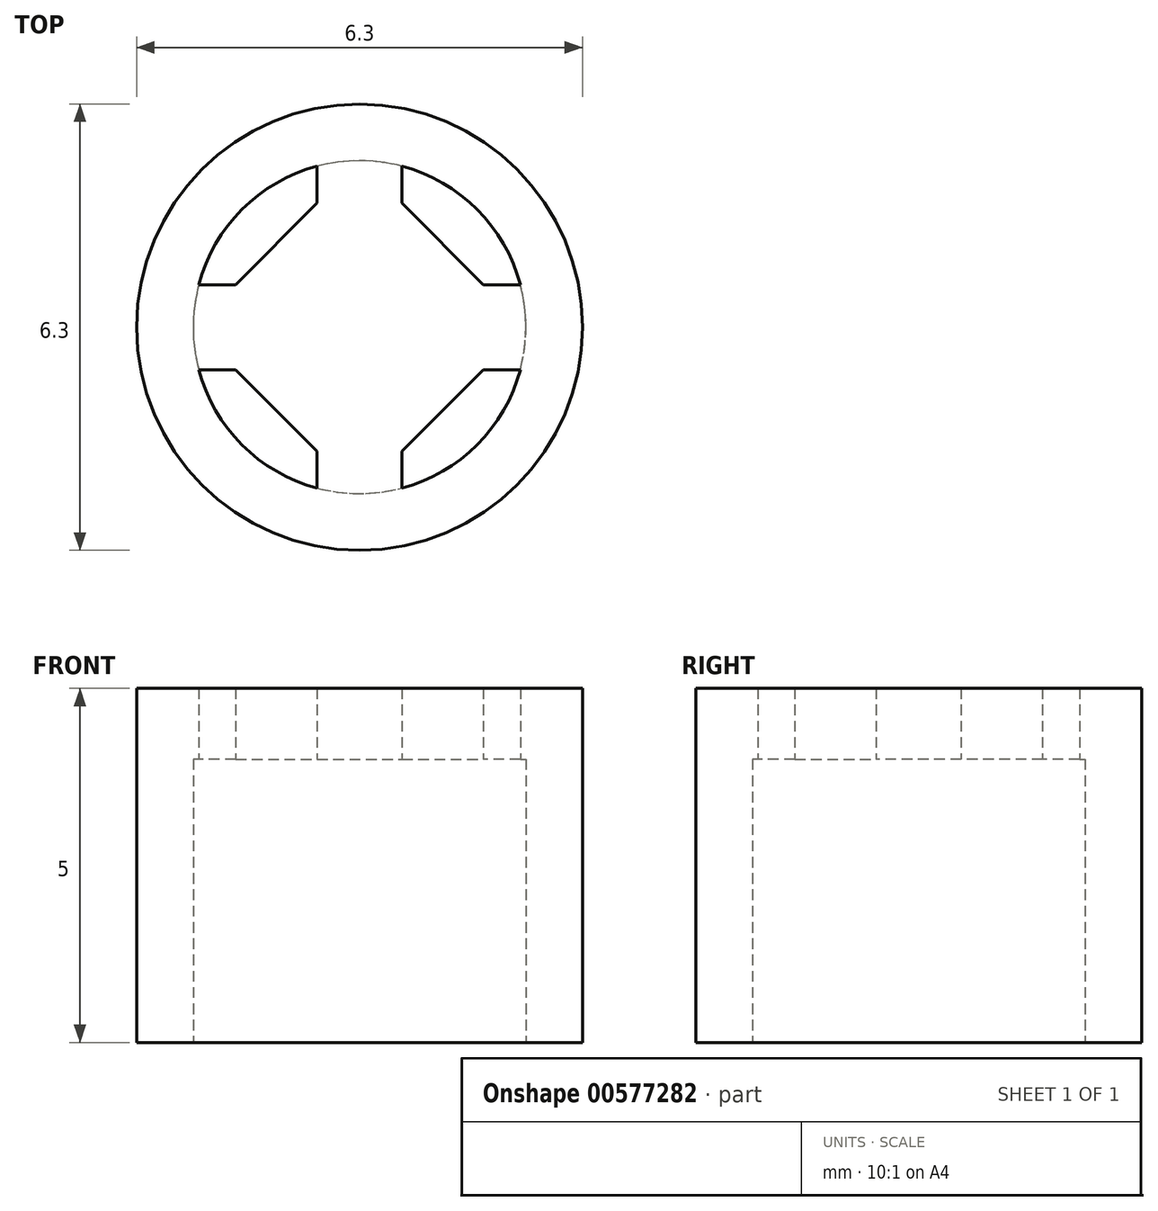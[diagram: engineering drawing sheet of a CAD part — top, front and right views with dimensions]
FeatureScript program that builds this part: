
annotation { "Feature Type Name" : "Feature", "Feature Type Description" : "" }
export const myFeature = defineFeature(function(context is Context, id is Id, definition is map)
    precondition{}
    {
        {
            var Q0;
            Q0=qCreatedBy(makeId("Top.planeOp"),FACE);
            var sketch = newSketch(context, id + "F0", { "sketchPlane" : qUnion([Q0])});
            skCircle(sketch, "E0", {"center": v(0, 0) * mm, "radius": 3.15 * mm});
            skCircle(sketch, "E1.0", {"center": v(0, 0) * mm, "radius": 2.35 * mm});
            skSolve(sketch);
        }
        {
            var Q0;
            Q0=makeQuery(id+"F0.imprint","IMPRINT",FACE,{"disambiguationData":[TD([[makeQuery(id+"F0.imprint","IMPRINT",EDGE,{"derivedFrom":sQuery(id+"F0.wireOp",EDGE,"E0")}),1.0]])]});
            extrude(context, id + "F1", {"entities" : qUnion([Q0]), "depth" : 4 * mm, "offsetDistance" : 25 * mm});
        }
        {
            var Q0;
            Q0=makeQuery(id+"F1.opExtrude","CAP_FACE",FACE,{"disambiguationData":[OSD([sQuery(id+"F0.wireOp",EDGE,"E0"),sQuery(id+"F0.wireOp",EDGE,"E1.0")])],"isStart":false});
            var sketch = newSketch(context, id + "F2", { "sketchPlane" : qUnion([Q0])});
            skArc(sketch, "E2.0", {"start": v(-0.6, 2.27) * mm, "mid": v(-1.66, 1.66) * mm, "end": v(-2.27, 0.6) * mm});
            skLineSegment(sketch, "E3", {"start": v(-0.6, 1.75) * mm, "end": v(-1.75, 0.6) * mm});
            skLineSegment(sketch, "E4", {"start": v(-1.75, -0.6) * mm, "end": v(-0.6, -1.75) * mm});
            skLineSegment(sketch, "E5", {"start": v(0.6, -1.75) * mm, "end": v(1.75, -0.6) * mm});
            skLineSegment(sketch, "E6", {"start": v(1.75, 0.6) * mm, "end": v(0.6, 1.75) * mm});
            skLineSegment(sketch, "E7.left", {"start": v(0.6, 2.27) * mm, "end": v(0.6, 1.75) * mm});
            skLineSegment(sketch, "E7.right", {"start": v(-0.6, 2.27) * mm, "end": v(-0.6, 1.75) * mm});
            skLineSegment(sketch, "E8.bottom", {"start": v(2.27, 0.6) * mm, "end": v(1.75, 0.6) * mm});
            skLineSegment(sketch, "E8.top", {"start": v(2.27, -0.6) * mm, "end": v(1.75, -0.6) * mm});
            skLineSegment(sketch, "E9.trimOffspring", {"start": v(-0.6, -1.75) * mm, "end": v(-0.6, -2.27) * mm});
            skLineSegment(sketch, "E10.trimOffspring", {"start": v(-1.75, 0.6) * mm, "end": v(-2.27, 0.6) * mm});
            skLineSegment(sketch, "E11.trimOffspring", {"start": v(0.6, -1.75) * mm, "end": v(0.6, -2.27) * mm});
            skLineSegment(sketch, "E12.trimOffspring", {"start": v(-1.75, -0.6) * mm, "end": v(-2.27, -0.6) * mm});
            skArc(sketch, "E13.trimOffspring", {"start": v(2.27, 0.6) * mm, "mid": v(1.66, 1.66) * mm, "end": v(0.6, 2.27) * mm});
            skArc(sketch, "E14.trimOffspring", {"start": v(0.6, -2.27) * mm, "mid": v(1.66, -1.66) * mm, "end": v(2.27, -0.6) * mm});
            skArc(sketch, "E15.trimOffspring", {"start": v(-2.27, -0.6) * mm, "mid": v(-1.66, -1.66) * mm, "end": v(-0.6, -2.27) * mm});
            skSolve(sketch);
        }
        {
            var Q0;
            Q0=makeQuery(id+"F2.imprint","IMPRINT",FACE,{"disambiguationData":[TD([[makeQuery(id+"F2.imprint","IMPRINT",EDGE,{"derivedFrom":sQuery(id+"F2.wireOp",EDGE,"E3")}),1.0]])]});
            var Q1;
            {var subQ3=sQuery(id+"F2.wireOp",EDGE,"E2.0");Q1=makeQuery(id+"F2.imprint","IMPRINT",FACE,{"disambiguationData":[TD([[makeQuery(id+"F2.imprint","IMPRINT",EDGE,{"derivedFrom":subQ3}),-1.0]])]});}
            extrude(context, id + "F3", {"entities" : qUnion([Q0, Q1]), "operationType" : NewBodyOperationType.ADD, "depth" : 1 * mm, "offsetDistance" : 25 * mm});
        }
        {
            var Q0;
            Q0=makeQuery(id+"F3.opExtrude","CAP_FACE",FACE,{"disambiguationData":[OSD([sQuery(id+"F0.wireOp",EDGE,"E0"),sQuery(id+"F2.wireOp",EDGE,"E2.0"),sQuery(id+"F2.wireOp",EDGE,"E3"),sQuery(id+"F2.wireOp",EDGE,"E4"),sQuery(id+"F2.wireOp",EDGE,"E5"),sQuery(id+"F2.wireOp",EDGE,"E6"),sQuery(id+"F2.wireOp",EDGE,"E7.left"),sQuery(id+"F2.wireOp",EDGE,"E7.right"),sQuery(id+"F2.wireOp",EDGE,"E8.bottom"),sQuery(id+"F2.wireOp",EDGE,"E8.top"),sQuery(id+"F2.wireOp",EDGE,"E9.trimOffspring"),sQuery(id+"F2.wireOp",EDGE,"E10.trimOffspring"),sQuery(id+"F2.wireOp",EDGE,"E11.trimOffspring"),sQuery(id+"F2.wireOp",EDGE,"E12.trimOffspring"),sQuery(id+"F2.wireOp",EDGE,"E13.trimOffspring"),sQuery(id+"F2.wireOp",EDGE,"E14.trimOffspring"),sQuery(id+"F2.wireOp",EDGE,"E15.trimOffspring")])],"isStart":false});
            cPlane(context, id + "F4", {"entities" : qUnion([Q0]), "cplaneType" : CPlaneType.OFFSET, "offset" : 3.7 * mm, "width" : 150 * mm, "height" : 150 * mm});
        }
    });
